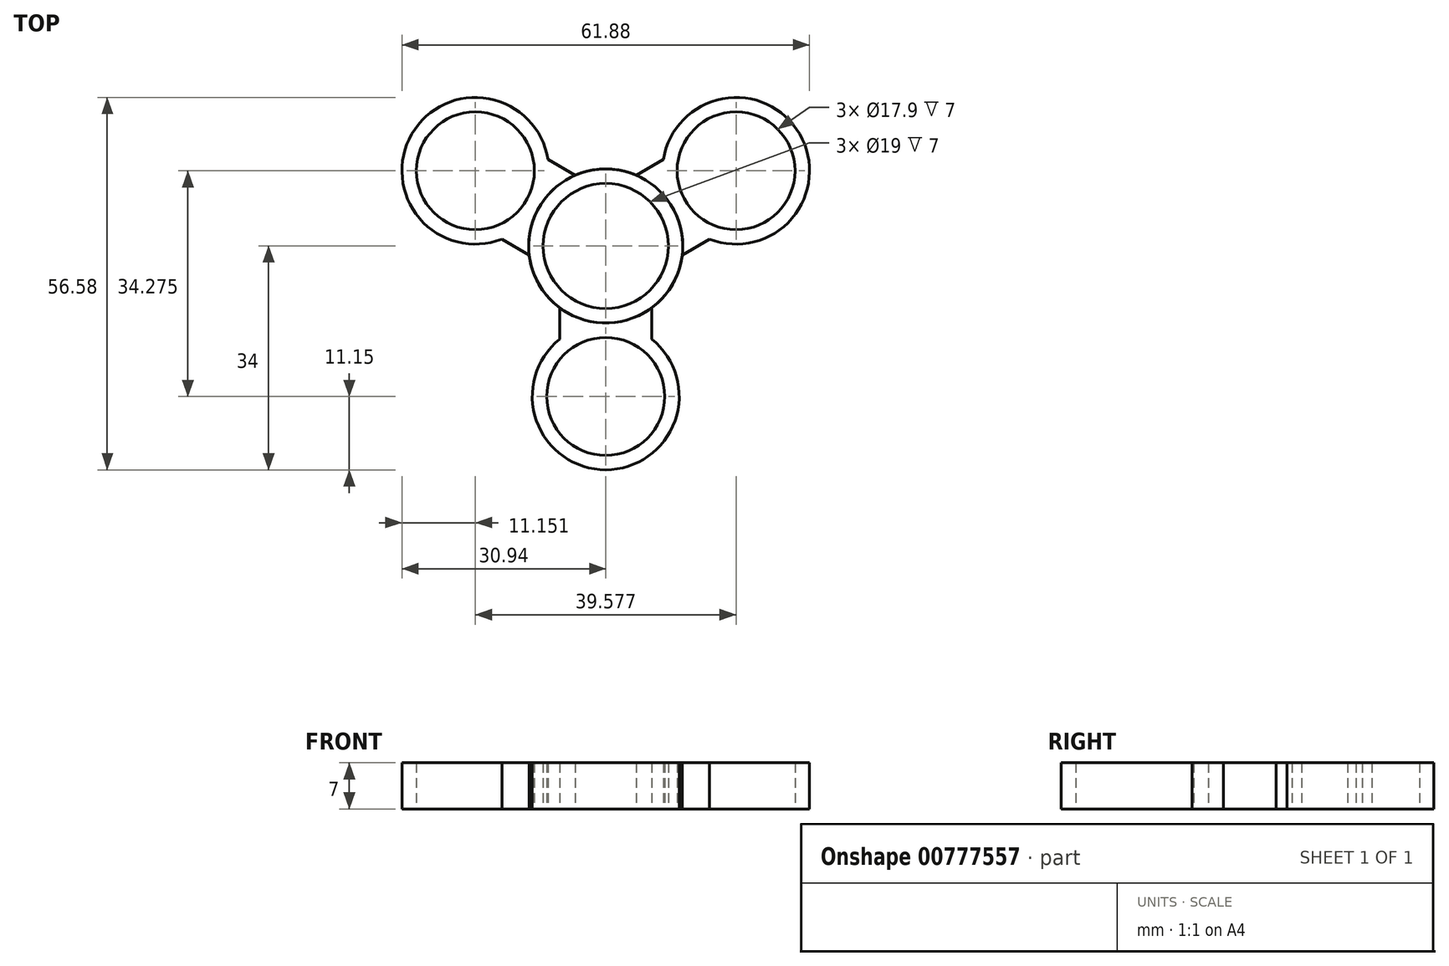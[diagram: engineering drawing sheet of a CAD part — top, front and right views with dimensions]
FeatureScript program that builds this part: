
annotation { "Feature Type Name" : "Feature", "Feature Type Description" : "" }
export const myFeature = defineFeature(function(context is Context, id is Id, definition is map)
    precondition{}
    {
        {
            var Q0;
            Q0=qCreatedBy(makeId("Top.planeOp"),FACE);
            var sketch = newSketch(context, id + "F0", { "sketchPlane" : qUnion([Q0])});
            skCircle(sketch, "E0", {"center": v(0, 0) * mm, "radius": 9.5 * mm});
            skCircle(sketch, "E1.0", {"center": v(0, 0) * mm, "radius": 11.7 * mm});
            skLineSegment(sketch, "E2.bottom", {"start": v(0, 0) * mm, "end": v(7, 0) * mm});
            skLineSegment(sketch, "E2.top", {"start": v(0, -22.85) * mm, "end": v(7, -22.85) * mm});
            skLineSegment(sketch, "E2.left", {"start": v(0, 0) * mm, "end": v(0, -22.85) * mm});
            skLineSegment(sketch, "E2.right", {"start": v(7, 0) * mm, "end": v(7, -22.85) * mm});
            skCircle(sketch, "E3", {"center": v(0, -22.85) * mm, "radius": 8.95 * mm});
            skCircle(sketch, "E4.0", {"center": v(0, -22.85) * mm, "radius": 11.15 * mm});
            skLineSegment(sketch, "E5.bottom", {"start": v(0, 0) * mm, "end": v(-7, 0) * mm});
            skLineSegment(sketch, "E5.top", {"start": v(0, -22.85) * mm, "end": v(-7, -22.85) * mm});
            skLineSegment(sketch, "E5.right", {"start": v(-7, 0) * mm, "end": v(-7, -22.85) * mm});
            skPoint(sketch, "E6", {"position": v(0, -11.7) * mm});
            skSolve(sketch);
        }
        {
            var Q0;
            {var subQ0=sQuery(id+"F0.wireOp",EDGE,"E4.0");var subQ1=sQuery(id+"F0.wireOp",EDGE,"E2.right");var subQ2=makeQuery(id+"F0.imprint","INTERSECT",VERTEX,{"derivedFrom":[subQ1,subQ0]});Q0=makeQuery(id+"F0.imprint","IMPRINT",FACE,{"disambiguationData":[TD([[makeQuery(id+"F0.imprint","IMPRINT",EDGE,{"disambiguationData":[TD([[subQ2,-1.0]])],"derivedFrom":subQ1}),1.0]])]});}
            var Q1;
            {var subQ0=sQuery(id+"F0.wireOp",EDGE,"E4.0");var subQ1=sQuery(id+"F0.wireOp",EDGE,"E2.right");var subQ2=makeQuery(id+"F0.imprint","INTERSECT",VERTEX,{"derivedFrom":[subQ1,subQ0]});Q1=makeQuery(id+"F0.imprint","IMPRINT",FACE,{"disambiguationData":[TD([[makeQuery(id+"F0.imprint","IMPRINT",EDGE,{"disambiguationData":[TD([[subQ2,-1.0]])],"derivedFrom":subQ1}),-1.0]])]});}
            var Q2;
            {var subQ0=sQuery(id+"F0.wireOp",EDGE,"E2.left");var subQ1=sQuery(id+"F0.wireOp",EDGE,"E3");var subQ2=makeQuery(id+"F0.imprint","INTERSECT",VERTEX,{"derivedFrom":[subQ1,subQ0]});Q2=makeQuery(id+"F0.imprint","IMPRINT",FACE,{"disambiguationData":[TD([[makeQuery(id+"F0.imprint","IMPRINT",EDGE,{"disambiguationData":[TD([[subQ2,-1.0]])],"derivedFrom":subQ1}),-1.0]])]});}
            var Q3;
            {var subQ0=sQuery(id+"F0.wireOp",EDGE,"E2.right");var subQ1=sQuery(id+"F0.wireOp",EDGE,"E1.0");var subQ2=makeQuery(id+"F0.imprint","INTERSECT",VERTEX,{"derivedFrom":[subQ1,subQ0]});Q3=makeQuery(id+"F0.imprint","IMPRINT",FACE,{"disambiguationData":[TD([[makeQuery(id+"F0.imprint","IMPRINT",EDGE,{"disambiguationData":[TD([[subQ2,1.0]])],"derivedFrom":subQ1}),-1.0]])]});}
            var Q4;
            {var subQ0=sQuery(id+"F0.wireOp",EDGE,"E5.right");var subQ1=sQuery(id+"F0.wireOp",EDGE,"E1.0");var subQ2=makeQuery(id+"F0.imprint","INTERSECT",VERTEX,{"derivedFrom":[subQ1,subQ0]});Q4=makeQuery(id+"F0.imprint","IMPRINT",FACE,{"disambiguationData":[TD([[makeQuery(id+"F0.imprint","IMPRINT",EDGE,{"disambiguationData":[TD([[subQ2,-1.0]])],"derivedFrom":subQ1}),-1.0]])]});}
            var Q5;
            {var subQ0=sQuery(id+"F0.wireOp",EDGE,"E2.left");var subQ1=sQuery(id+"F0.wireOp",EDGE,"E0");var subQ2=makeQuery(id+"F0.imprint","INTERSECT",VERTEX,{"derivedFrom":[subQ1,subQ0]});Q5=makeQuery(id+"F0.imprint","IMPRINT",FACE,{"disambiguationData":[TD([[makeQuery(id+"F0.imprint","IMPRINT",EDGE,{"disambiguationData":[TD([[subQ2,1.0]])],"derivedFrom":subQ1}),-1.0]])]});}
            var Q6;
            {var subQ0=sQuery(id+"F0.wireOp",EDGE,"E2.left");var subQ1=sQuery(id+"F0.wireOp",EDGE,"E0");var subQ2=makeQuery(id+"F0.imprint","INTERSECT",VERTEX,{"derivedFrom":[subQ1,subQ0]});Q6=makeQuery(id+"F0.imprint","IMPRINT",FACE,{"disambiguationData":[TD([[makeQuery(id+"F0.imprint","IMPRINT",EDGE,{"disambiguationData":[TD([[subQ2,-1.0]])],"derivedFrom":subQ1}),-1.0]])]});}
            var Q7;
            {var subQ0=sQuery(id+"F0.wireOp",EDGE,"E5.right");var subQ1=sQuery(id+"F0.wireOp",EDGE,"E0");var subQ2=makeQuery(id+"F0.imprint","INTERSECT",VERTEX,{"derivedFrom":[subQ1,subQ0]});Q7=makeQuery(id+"F0.imprint","IMPRINT",FACE,{"disambiguationData":[TD([[makeQuery(id+"F0.imprint","IMPRINT",EDGE,{"disambiguationData":[TD([[subQ2,1.0]])],"derivedFrom":subQ1}),-1.0]])]});}
            extrude(context, id + "F1", {"entities" : qUnion([Q0, Q1, Q2, Q3, Q4, Q5, Q6, Q7]), "depth" : 7 * mm, "offsetDistance" : 25 * mm});
        }
        {
            var Q0;
            Q0=makeQuery(id+"F1.opExtrude","SWEPT_BODY",BODY,{"disambiguationData":[OSD([sQuery(id+"F0.wireOp",EDGE,"E0"),sQuery(id+"F0.wireOp",EDGE,"E1.0"),sQuery(id+"F0.wireOp",EDGE,"E2.right"),sQuery(id+"F0.wireOp",EDGE,"E3"),sQuery(id+"F0.wireOp",EDGE,"E4.0"),sQuery(id+"F0.wireOp",EDGE,"E5.right")])]});
            var Q1;
            Q1=makeQuery(id+"F1.opExtrude","CAP_EDGE",EDGE,{"disambiguationData":[OSD([sQuery(id+"F0.wireOp",EDGE,"E0")])],"isStart":false});
            circularPattern(context, id + "F2", {"entities" : qUnion([Q0]), "axis" : qUnion([Q1]), "angle" : 360 * degree, "instanceCount" : 3, "equalSpace" : true});
        }
    });
